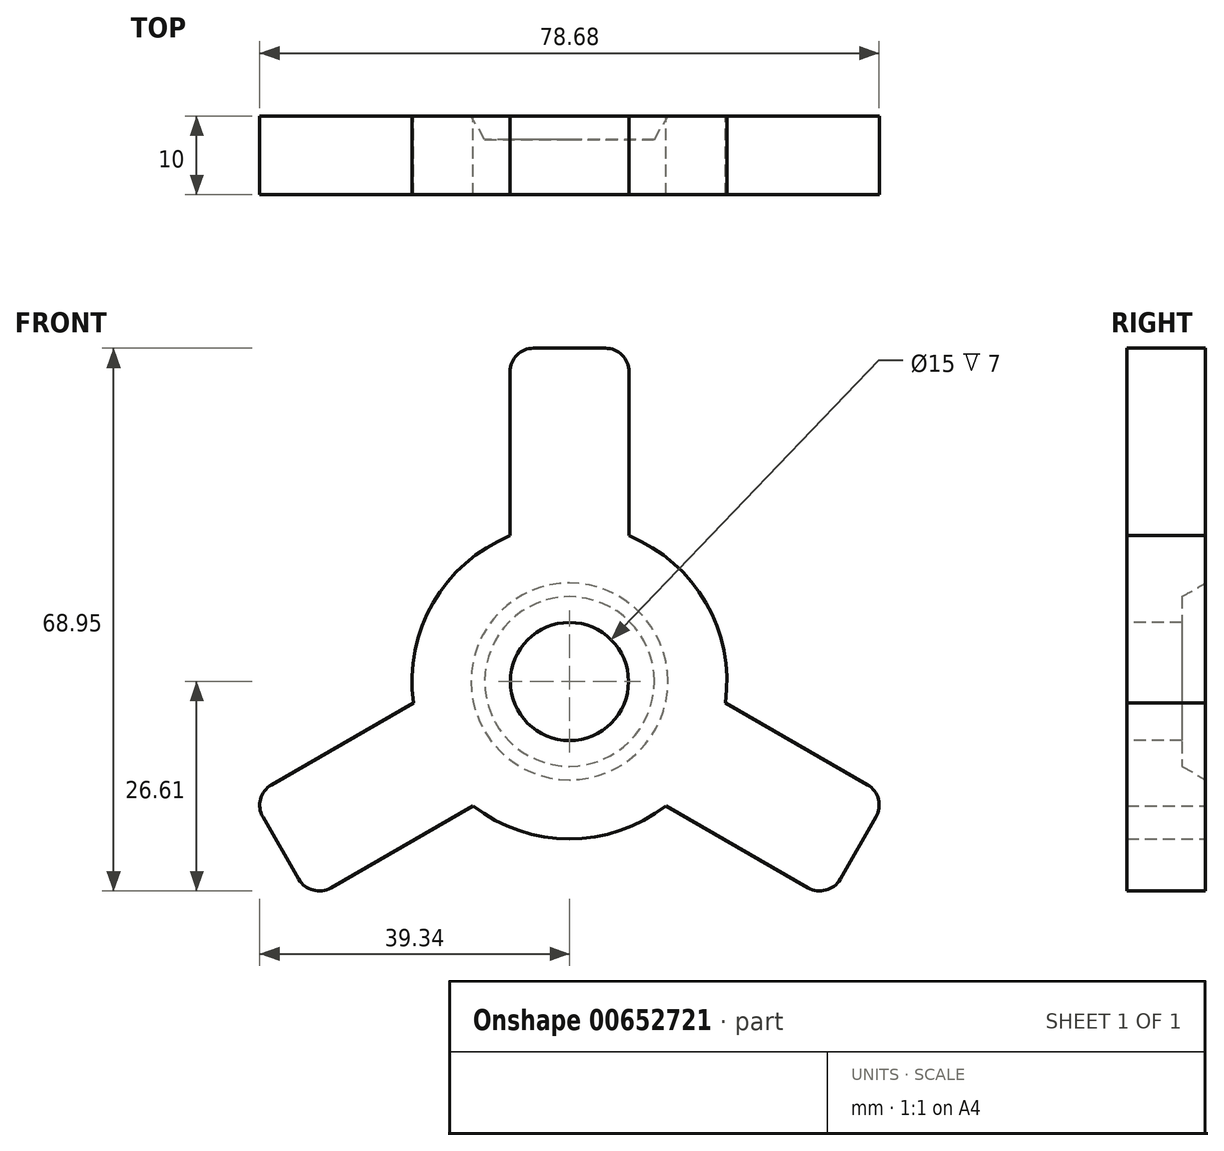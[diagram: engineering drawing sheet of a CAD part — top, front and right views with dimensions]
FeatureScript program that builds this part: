
annotation { "Feature Type Name" : "Feature", "Feature Type Description" : "" }
export const myFeature = defineFeature(function(context is Context, id is Id, definition is map)
    precondition{}
    {
        {
            var Q0;
            Q0=qCreatedBy(makeId("Front.planeOp"),FACE);
            var sketch = newSketch(context, id + "F0", { "sketchPlane" : qUnion([Q0])});
            skCircle(sketch, "E0", {"center": v(0, 0) * mm, "radius": 20 * mm});
            skLineSegment(sketch, "E1.bottom", {"start": v(7.55, 18.52) * mm, "end": v(-7.55, 18.52) * mm});
            skLineSegment(sketch, "E1.top", {"start": v(7.55, 42.34) * mm, "end": v(-7.55, 42.34) * mm});
            skLineSegment(sketch, "E1.left", {"start": v(7.55, 18.52) * mm, "end": v(7.55, 42.34) * mm});
            skLineSegment(sketch, "E1.right", {"start": v(-7.55, 18.52) * mm, "end": v(-7.55, 42.34) * mm});
            skPoint(sketch, "E1.middle", {"position": v(0, 30.43) * mm});
            skLineSegment(sketch, "E2.1.0", {"start": v(-40.44, -14.63) * mm, "end": v(-32.9, -27.7) * mm});
            skLineSegment(sketch, "E2.1.1", {"start": v(-12.26, -15.8) * mm, "end": v(-32.9, -27.7) * mm});
            skLineSegment(sketch, "E2.1.2", {"start": v(-19.81, -2.72) * mm, "end": v(-40.44, -14.63) * mm});
            skLineSegment(sketch, "E2.1.3", {"start": v(-19.81, -2.72) * mm, "end": v(-12.26, -15.8) * mm});
            skLineSegment(sketch, "E2.2.0", {"start": v(32.9, -27.7) * mm, "end": v(40.44, -14.63) * mm});
            skLineSegment(sketch, "E2.2.1", {"start": v(19.81, -2.72) * mm, "end": v(40.44, -14.63) * mm});
            skLineSegment(sketch, "E2.2.2", {"start": v(12.26, -15.8) * mm, "end": v(32.9, -27.7) * mm});
            skLineSegment(sketch, "E2.2.3", {"start": v(12.26, -15.8) * mm, "end": v(19.81, -2.72) * mm});
            skSolve(sketch);
        }
        {
            var Q0;
            Q0 = qSketchRegion(id + "F0", true);
            extrude(context, id + "F1", {"entities" : qUnion([Q0]), "endBound" : BoundingType.SYMMETRIC, "depth" : 10 * mm, "offsetDistance" : 25 * mm});
        }
        {
            var Q0;
            Q0=makeQuery(id+"F1.opExtrude","CAP_FACE",FACE,{"disambiguationData":[OSD([sQuery(id+"F0.wireOp",EDGE,"E0"),sQuery(id+"F0.wireOp",EDGE,"E1.top"),sQuery(id+"F0.wireOp",EDGE,"E1.left"),sQuery(id+"F0.wireOp",EDGE,"E1.right"),sQuery(id+"F0.wireOp",EDGE,"E2.1.0"),sQuery(id+"F0.wireOp",EDGE,"E2.1.1"),sQuery(id+"F0.wireOp",EDGE,"E2.1.2"),sQuery(id+"F0.wireOp",EDGE,"E2.2.0"),sQuery(id+"F0.wireOp",EDGE,"E2.2.1"),sQuery(id+"F0.wireOp",EDGE,"E2.2.2")])],"isStart":true});
            var sketch = newSketch(context, id + "F2", { "sketchPlane" : qUnion([Q0])});
            skCircle(sketch, "E3", {"center": v(0, 0) * mm, "radius": 12.5 * mm});
            skSolve(sketch);
        }
        {
            var Q0;
            Q0 = qSketchRegion(id + "F2", true);
            extrude(context, id + "F3", {"entities" : qUnion([Q0]), "operationType" : NewBodyOperationType.REMOVE, "oppositeDirection" : true, "depth" : 3 * mm, "offsetDistance" : 25 * mm, "hasDraft" : true, "draftAngle" : 30 * degree, "draftPullDirection" : true});
        }
        {
            var Q0;
            Q0=qCreatedBy(makeId("Front.planeOp"),FACE);
            var sketch = newSketch(context, id + "F4", { "sketchPlane" : qUnion([Q0])});
            skCircle(sketch, "E4", {"center": v(0, 0) * mm, "radius": 7.5 * mm});
            skSolve(sketch);
        }
        {
            var Q0;
            Q0 = qSketchRegion(id + "F4", true);
            extrude(context, id + "F5", {"entities" : qUnion([Q0]), "operationType" : NewBodyOperationType.REMOVE, "endBound" : BoundingType.THROUGH_ALL, "oppositeDirection" : true, "depth" : 25 * mm, "offsetDistance" : 25 * mm});
        }
        {
            var Q0;
            Q0=makeQuery(id+"F5.boolean.opBoolean","COPY",FACE,{"derivedFrom":makeQuery(id+"F5.opExtrude","CAP_FACE",FACE,{"disambiguationData":[OSD([sQuery(id+"F4.wireOp",EDGE,"E4")])],"isStart":true})});
            extrude(context, id + "F6", {"entities" : qUnion([Q0]), "operationType" : NewBodyOperationType.REMOVE, "endBound" : BoundingType.THROUGH_ALL, "oppositeDirection" : true, "depth" : 25 * mm, "offsetDistance" : 25 * mm});
        }
        {
            var Q0;
            Q0=makeQuery(id+"F1.opExtrude","SWEPT_EDGE",EDGE,{"disambiguationData":[OSD([sQuery(id+"F0.wireOp",EDGE,"E1.top"),sQuery(id+"F0.wireOp",EDGE,"E1.right")])]});
            var Q1;
            Q1=makeQuery(id+"F1.opExtrude","SWEPT_EDGE",EDGE,{"disambiguationData":[OSD([sQuery(id+"F0.wireOp",EDGE,"E1.top"),sQuery(id+"F0.wireOp",EDGE,"E1.left")])]});
            var Q2;
            Q2=makeQuery(id+"F1.opExtrude","SWEPT_EDGE",EDGE,{"disambiguationData":[OSD([sQuery(id+"F0.wireOp",EDGE,"E2.2.0"),sQuery(id+"F0.wireOp",EDGE,"E2.2.1")])]});
            var Q3;
            Q3=makeQuery(id+"F1.opExtrude","SWEPT_EDGE",EDGE,{"disambiguationData":[OSD([sQuery(id+"F0.wireOp",EDGE,"E2.2.0"),sQuery(id+"F0.wireOp",EDGE,"E2.2.2")])]});
            var Q4;
            Q4=makeQuery(id+"F1.opExtrude","SWEPT_EDGE",EDGE,{"disambiguationData":[OSD([sQuery(id+"F0.wireOp",EDGE,"E2.1.0"),sQuery(id+"F0.wireOp",EDGE,"E2.1.1")])]});
            var Q5;
            Q5=makeQuery(id+"F1.opExtrude","SWEPT_EDGE",EDGE,{"disambiguationData":[OSD([sQuery(id+"F0.wireOp",EDGE,"E2.1.0"),sQuery(id+"F0.wireOp",EDGE,"E2.1.2")])]});
            fillet(context, id + "F7", {"entities" : qUnion([Q0, Q1, Q2, Q3, Q4, Q5]), "radius" : 3 * mm, "tangentPropagation" : true, "allowEdgeOverflow" : false});
        }
    });
